# Revit family: CU2SQ
name_source: partatom
category: Lighting Fixtures
revit_build: Autodesk Revit 2014 (Build: 20130308_1515(x64)
units: mm (PartAtom-declared; Revit-internal decimal feet)

## types (2) — shared parameters
Apparent Load = 4 VA
Application = The CU2SQ Series can be applied in stair-wells, hallways,
offices and commercial applications.
Certification = UL924 Listed for Damp Location
NFPA 101 and NFPA 70
OSHA
Default Elevation = 48 "
Description = The CU2SQ Series offers quality and value with a compact and attractive LED based emergency light. The white or black housing and lamp-heads are made of high impact UL flame rated thermoplastic. The square LED lamp-heads are fully adjustable and glare-free. Snap together design for quick and easy installation with option of wall or ceiling mount. The remote capacity unit will run 2 Compass CIR/COR Series single remote lamp-heads or 1 double CIR/COR remote.
Features = LED life-cycle of more than 10 years
•	 Quick installation
•	 Dual-voltage 120 or 277V AC input
•	 Includes long-life Nickel Cadmium battery for UL
recognized 90 minute emergency lighting
•	 Remote capacity or extended runtime option
•	 Damp Location Listed 20°C to 30°C (68°F to 86°F)
•	 Fully adjustable lamp-heads
•	 Provided with test switch and AC-On indicator
•	 Remote Capacity (RC) models and AC-On indicator
•	 Wall or Ceiling mount
•	 Remote Capacity (RC) Models have a minimum runtime
of 120 minutes when no remotes are installed
Glass = Hubbell- White Glass
LED = Hubbell- White Glass
Lamp = LED Lamp
Manufacturer = Compass Lighting
Nominal Watts = 4 W
Product Documentation Link = https://hubbellcdn.com
Product Page URL = https://www.hubbell.com
Steel = Metal-Hubbell-Galvanized_Steel
URL = https://www.hubbell.com
Voltage = 120 V
Warranty = 2Year full unit warranty
Wattage Comments = 3.6W

## per-type parameters (varying)
| type | Backbox |
| CU2SQ | Hubbell- Paint- White |
| CU2SQB | Hubbell- Paint- Black Matte Textured |

note: column(s) folded — value = type name in every type: Model

## geometry (parser evidence)
native form markers: Blend x23, Sweep x2
no freeform markers — native parametric forms only
